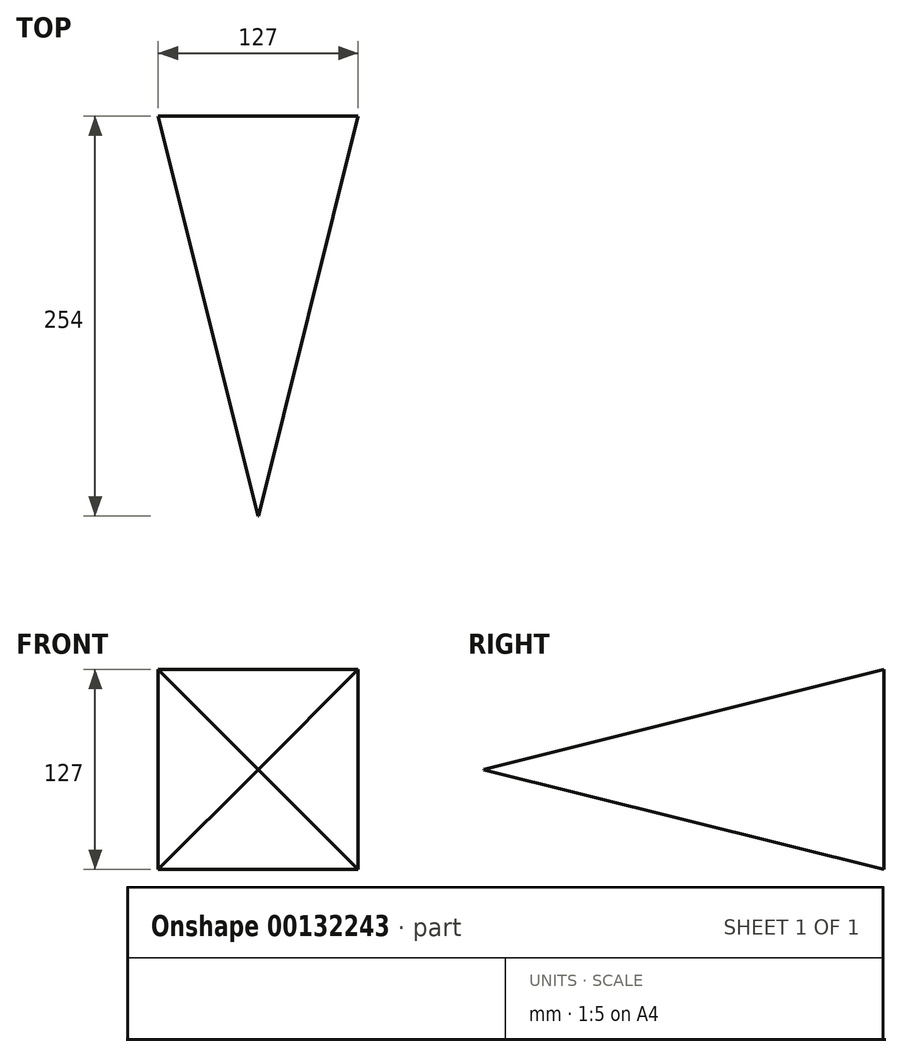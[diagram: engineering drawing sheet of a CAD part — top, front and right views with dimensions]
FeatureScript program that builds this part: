
annotation { "Feature Type Name" : "Feature", "Feature Type Description" : "" }
export const myFeature = defineFeature(function(context is Context, id is Id, definition is map)
    precondition{}
    {
        {
            var Q0;
            Q0=qCreatedBy(makeId("Front.planeOp"),FACE);
            var sketch = newSketch(context, id + "F0", { "sketchPlane" : qUnion([Q0])});
            skLineSegment(sketch, "E0.bottom", {"start": v(63.5, 63.5) * mm, "end": v(-63.5, 63.5) * mm});
            skLineSegment(sketch, "E0.top", {"start": v(63.5, -63.5) * mm, "end": v(-63.5, -63.5) * mm});
            skLineSegment(sketch, "E0.left", {"start": v(63.5, 63.5) * mm, "end": v(63.5, -63.5) * mm});
            skLineSegment(sketch, "E0.right", {"start": v(-63.5, 63.5) * mm, "end": v(-63.5, -63.5) * mm});
            skPoint(sketch, "E0.middle", {"position": v(0, 0) * mm});
            skSolve(sketch);
        }
        {
            var Q0;
            Q0 = qSketchRegion(id + "F0", true);
            extrude(context, id + "F1", {"entities" : qUnion([Q0]), "depth" : 254 * mm, "hasDraft" : true, "draftAngle" : 14 * degree, "draftPullDirection" : true});
        }
    });
